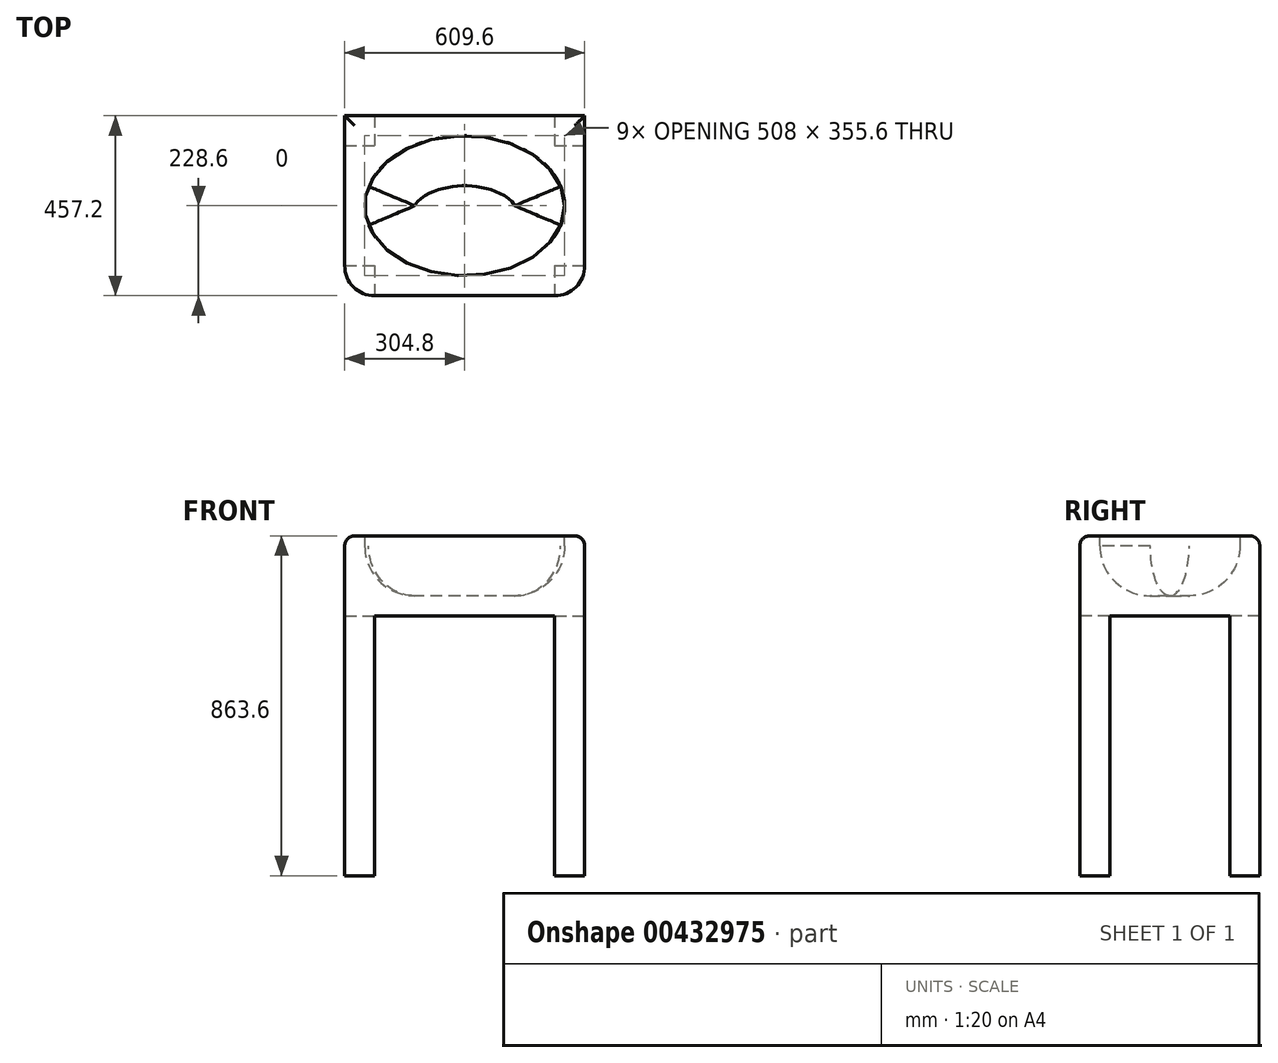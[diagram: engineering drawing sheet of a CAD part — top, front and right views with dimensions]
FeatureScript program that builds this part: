
annotation { "Feature Type Name" : "Feature", "Feature Type Description" : "" }
export const myFeature = defineFeature(function(context is Context, id is Id, definition is map)
    precondition{}
    {
        {
            var Q0;
            Q0=qCreatedBy(makeId("Top.planeOp"),FACE);
            var sketch = newSketch(context, id + "F0", { "sketchPlane" : qUnion([Q0])});
            skLineSegment(sketch, "E0.bottom", {"start": v(304.8, 228.6) * mm, "end": v(-304.8, 228.6) * mm});
            skLineSegment(sketch, "E0.top", {"start": v(304.8, -228.6) * mm, "end": v(-304.8, -228.6) * mm});
            skLineSegment(sketch, "E0.left", {"start": v(304.8, 228.6) * mm, "end": v(304.8, -228.6) * mm});
            skLineSegment(sketch, "E0.right", {"start": v(-304.8, 228.6) * mm, "end": v(-304.8, -228.6) * mm});
            skPoint(sketch, "E0.middle", {"position": v(0, 0) * mm});
            skSolve(sketch);
        }
        {
            var Q0;
            Q0=makeQuery(id+"F0.imprint","IMPRINT",FACE,{"disambiguationData":[TD([[makeQuery(id+"F0.imprint","IMPRINT",EDGE,{"derivedFrom":sQuery(id+"F0.wireOp",EDGE,"E0.bottom")}),1.0]])]});
            extrude(context, id + "F1", {"entities" : qUnion([Q0]), "depth" : 863.6 * mm});
        }
        {
            var Q0;
            Q0=makeQuery(id+"F1.opExtrude","SWEPT_EDGE",EDGE,{"disambiguationData":[OSD([sQuery(id+"F0.wireOp",EDGE,"E0.top"),sQuery(id+"F0.wireOp",EDGE,"E0.right")])]});
            var Q1;
            Q1=makeQuery(id+"F1.opExtrude","SWEPT_EDGE",EDGE,{"disambiguationData":[OSD([sQuery(id+"F0.wireOp",EDGE,"E0.top"),sQuery(id+"F0.wireOp",EDGE,"E0.left")])]});
            fillet(context, id + "F2", {"entities" : qUnion([Q0, Q1]), "radius" : 76.2 * mm, "tangentPropagation" : true, "allowEdgeOverflow" : false});
        }
        {
            var Q0;
            Q0=makeQuery(id+"F1.opExtrude","SWEPT_FACE",FACE,{"disambiguationData":[OSD([sQuery(id+"F0.wireOp",EDGE,"E0.top")])]});
            var sketch = newSketch(context, id + "F3", { "sketchPlane" : qUnion([Q0])});
            skLineSegment(sketch, "E1", {"start": v(-228.6, 0) * mm, "end": v(-228.6, 660.4) * mm});
            skLineSegment(sketch, "E2", {"start": v(-228.6, 660.4) * mm, "end": v(228.6, 660.4) * mm});
            skLineSegment(sketch, "E3", {"start": v(228.6, 660.4) * mm, "end": v(228.6, 0) * mm});
            skLineSegment(sketch, "E4", {"start": v(228.6, 0) * mm, "end": v(-228.6, 0) * mm});
            skSolve(sketch);
        }
        {
            var Q0;
            Q0=makeQuery(id+"F3.imprint","IMPRINT",FACE,{"disambiguationData":[TD([[makeQuery(id+"F3.imprint","IMPRINT",EDGE,{"derivedFrom":sQuery(id+"F3.wireOp",EDGE,"E1")}),1.0]])]});
            extrude(context, id + "F4", {"entities" : qUnion([Q0]), "operationType" : NewBodyOperationType.REMOVE, "endBound" : BoundingType.THROUGH_ALL, "oppositeDirection" : true, "depth" : 25.4 * mm});
        }
        {
            var Q0;
            Q0=makeQuery(id+"F1.opExtrude","SWEPT_FACE",FACE,{"disambiguationData":[OSD([sQuery(id+"F0.wireOp",EDGE,"E0.left")])]});
            var sketch = newSketch(context, id + "F5", { "sketchPlane" : qUnion([Q0])});
            skLineSegment(sketch, "E5", {"start": v(-152.4, 0) * mm, "end": v(-152.4, 660.4) * mm});
            skLineSegment(sketch, "E6", {"start": v(-152.4, 660.4) * mm, "end": v(152.4, 660.4) * mm});
            skLineSegment(sketch, "E7", {"start": v(152.4, 660.4) * mm, "end": v(152.4, 0) * mm});
            skLineSegment(sketch, "E8", {"start": v(152.4, 0) * mm, "end": v(-152.4, 0) * mm});
            skSolve(sketch);
        }
        {
            var Q0;
            Q0=makeQuery(id+"F5.imprint","IMPRINT",FACE,{"disambiguationData":[TD([[makeQuery(id+"F5.imprint","IMPRINT",EDGE,{"derivedFrom":sQuery(id+"F5.wireOp",EDGE,"E5")}),1.0]])]});
            extrude(context, id + "F6", {"entities" : qUnion([Q0]), "operationType" : NewBodyOperationType.REMOVE, "endBound" : BoundingType.THROUGH_ALL, "oppositeDirection" : true, "depth" : 25.4 * mm});
        }
        {
            var Q0;
            Q0=makeQuery(id+"F1.opExtrude","CAP_FACE",FACE,{"disambiguationData":[OSD([sQuery(id+"F0.wireOp",EDGE,"E0.bottom"),sQuery(id+"F0.wireOp",EDGE,"E0.top"),sQuery(id+"F0.wireOp",EDGE,"E0.left"),sQuery(id+"F0.wireOp",EDGE,"E0.right")])],"isStart":false});
            var sketch = newSketch(context, id + "F7", { "sketchPlane" : qUnion([Q0])});
            skEllipse(sketch, "E9", {"center": v(0, 0) * mm, "majorRadius": 254 * mm, "minorRadius": 177.8 * mm, "majorAxis": v(1, 0)});
            skSolve(sketch);
        }
        {
            var Q0;
            Q0=makeQuery(id+"F7.imprint","IMPRINT",FACE,{"disambiguationData":[TD([[makeQuery(id+"F7.imprint","IMPRINT",EDGE,{"derivedFrom":sQuery(id+"F7.wireOp",EDGE,"E9")}),1.0]])]});
            extrude(context, id + "F8", {"entities" : qUnion([Q0]), "operationType" : NewBodyOperationType.REMOVE, "oppositeDirection" : true, "depth" : 152.4 * mm});
        }
        {
            var Q0;
            Q0=makeQuery(id+"F8.boolean.opBoolean","COPY",EDGE,{"derivedFrom":makeQuery(id+"F8.opExtrude","CAP_EDGE",EDGE,{"disambiguationData":[OSD([sQuery(id+"F7.wireOp",EDGE,"E9")])],"isStart":false})});
            fillet(context, id + "F9", {"entities" : qUnion([Q0]), "radius" : 127 * mm, "tangentPropagation" : true, "allowEdgeOverflow" : false});
        }
        {
            var Q0;
            Q0=makeQuery(id+"F1.opExtrude","CAP_EDGE",EDGE,{"disambiguationData":[OSD([sQuery(id+"F0.wireOp",EDGE,"E0.top")])],"isStart":false});
            var Q1;
            {var subQ0=sQuery(id+"F0.wireOp",EDGE,"E0.left");var subQ1=sQuery(id+"F0.wireOp",EDGE,"E0.top");Q1=makeQuery(id+"F2.opFillet","BLEND_EDGE",EDGE,{"blendedFrom":[makeQuery(id+"F1.opExtrude","SWEPT_EDGE",EDGE,{"disambiguationData":[OSD([subQ1,subQ0])]}),makeQuery(id+"F1.opExtrude","CAP_FACE",FACE,{"disambiguationData":[OSD([sQuery(id+"F0.wireOp",EDGE,"E0.bottom"),subQ1,subQ0,sQuery(id+"F0.wireOp",EDGE,"E0.right")])],"isStart":false})],"blendedInto":[makeQuery(id+"F1.opExtrude","CAP_FACE",FACE,{"disambiguationData":[OSD([sQuery(id+"F0.wireOp",EDGE,"E0.bottom"),subQ1,subQ0,sQuery(id+"F0.wireOp",EDGE,"E0.right")])],"isStart":false})]});}
            var Q2;
            Q2=makeQuery(id+"F1.opExtrude","CAP_EDGE",EDGE,{"disambiguationData":[OSD([sQuery(id+"F0.wireOp",EDGE,"E0.left")])],"isStart":false});
            var Q3;
            Q3=makeQuery(id+"F1.opExtrude","CAP_EDGE",EDGE,{"disambiguationData":[OSD([sQuery(id+"F0.wireOp",EDGE,"E0.bottom")])],"isStart":false});
            var Q4;
            Q4=makeQuery(id+"F1.opExtrude","CAP_EDGE",EDGE,{"disambiguationData":[OSD([sQuery(id+"F0.wireOp",EDGE,"E0.right")])],"isStart":false});
            var Q5;
            {var subQ0=sQuery(id+"F0.wireOp",EDGE,"E0.right");var subQ1=sQuery(id+"F0.wireOp",EDGE,"E0.top");Q5=makeQuery(id+"F2.opFillet","BLEND_EDGE",EDGE,{"blendedFrom":[makeQuery(id+"F1.opExtrude","SWEPT_EDGE",EDGE,{"disambiguationData":[OSD([subQ1,subQ0])]}),makeQuery(id+"F1.opExtrude","CAP_FACE",FACE,{"disambiguationData":[OSD([sQuery(id+"F0.wireOp",EDGE,"E0.bottom"),subQ1,sQuery(id+"F0.wireOp",EDGE,"E0.left"),subQ0])],"isStart":false})],"blendedInto":[makeQuery(id+"F1.opExtrude","CAP_FACE",FACE,{"disambiguationData":[OSD([sQuery(id+"F0.wireOp",EDGE,"E0.bottom"),subQ1,sQuery(id+"F0.wireOp",EDGE,"E0.left"),subQ0])],"isStart":false})]});}
            fillet(context, id + "F10", {"entities" : qUnion([Q0, Q1, Q2, Q3, Q4, Q5]), "radius" : 25.4 * mm, "tangentPropagation" : true, "allowEdgeOverflow" : false});
        }
    });
